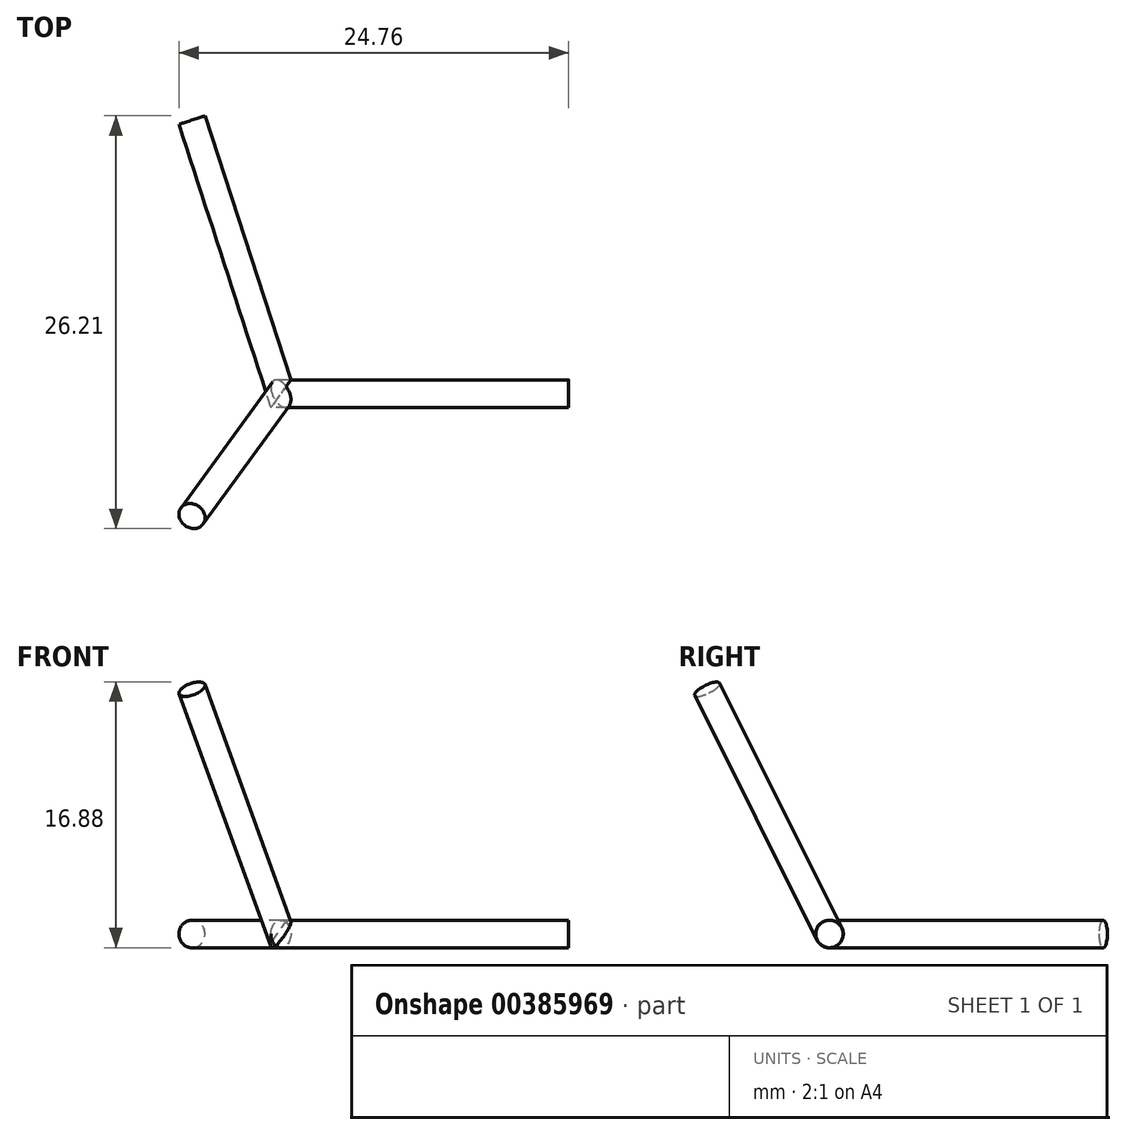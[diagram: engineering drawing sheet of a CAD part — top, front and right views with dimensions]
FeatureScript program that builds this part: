
annotation { "Feature Type Name" : "Feature", "Feature Type Description" : "" }
export const myFeature = defineFeature(function(context is Context, id is Id, definition is map)
    precondition{}
    {
        {
            var Q0;
            Q0=qCreatedBy(makeId("Top.planeOp"),FACE);
            var sketch = newSketch(context, id + "F0", { "sketchPlane" : qUnion([Q0])});
            skCircle(sketch, "E0.cCircle", {"center": v(0, 0) * mm, "radius": 15.55 * mm, "construction": true});
            skLineSegment(sketch, "E0.2", {"start": v(9.14, -12.58) * mm, "end": v(-9.14, -12.58) * mm});
            skPoint(sketch, "E0.4.end.orphan", {"position": v(0, 15.55) * mm});
            skLineSegment(sketch, "E1", {"start": v(9.14, -12.58) * mm, "end": v(9.14, -22.73) * mm, "construction": true});
            skLineSegment(sketch, "E2.1", {"start": v(-9.14, -12.58) * mm, "end": v(-14.79, 4.8) * mm});
            skSolve(sketch);
        }
        {
            var Q0;
            Q0=sQuery(id+"F0.wireOp",EDGE,"E1");
            cPlane(context, id + "F1", {"entities" : qUnion([Q0]), "cplaneType" : CPlaneType.LINE_ANGLE, "offset" : 25 * mm, "angle" : 90 * degree, "width" : 150 * mm, "height" : 150 * mm});
        }
        {
            var Q0;
            Q0=qCreatedBy(id+"F1.planeOp",FACE);
            var sketch = newSketch(context, id + "F2", { "sketchPlane" : qUnion([Q0])});
            skPoint(sketch, "E3.0", {"position": v(-12.58, 0) * mm});
            skCircle(sketch, "E4", {"center": v(-12.58, 0) * mm, "radius": 0.87 * mm});
            skSolve(sketch);
        }
        {
            var Q0;
            Q0=makeQuery(id+"F2.imprint","IMPRINT",FACE,{"disambiguationData":[TD([[makeQuery(id+"F2.imprint","IMPRINT",EDGE,{"derivedFrom":sQuery(id+"F2.wireOp",EDGE,"E4")}),1.0]])]});
            var Q1;
            Q1=sQuery(id+"F0.wireOp",EDGE,"E0.2");
            var Q2;
            Q2=sQuery(id+"F0.wireOp",EDGE,"E2.1");
            sweep(context, id + "F3", {"profiles" : qUnion([Q0]), "path" : qUnion([Q1, Q2])});
        }
        {
            var Q0;
            Q0=makeQuery(id+"F3.opSweep","SWEPT_BODY",BODY,{"disambiguationData":[OSD([sQuery(id+"F0.wireOp",EDGE,"E2.1"),sQuery(id+"F2.wireOp",EDGE,"E4")])]});
            var Q1;
            Q1=makeQuery(id+"F3.opSweep","CAP_EDGE",EDGE,{"disambiguationData":[OSD([sQuery(id+"F0.wireOp",VERTEX,"E0.2.start"),sQuery(id+"F2.wireOp",EDGE,"E4")])],"isStart":true});
            var Q2;
            Q2=makeQuery(id+"F3.opSweep","SWEPT_FACE",FACE,{"disambiguationData":[OSD([sQuery(id+"F0.wireOp",EDGE,"E0.2"),sQuery(id+"F2.wireOp",EDGE,"E4")])]});
            transform(context, id + "F4", {"entities" : qUnion([Q0]), "transformType" : TransformType.ROTATION, "transformAxis" : qUnion([Q2]), "angle" : 116.56 * degree, "oppositeDirection" : true, "makeCopy" : true});
        }
    });
